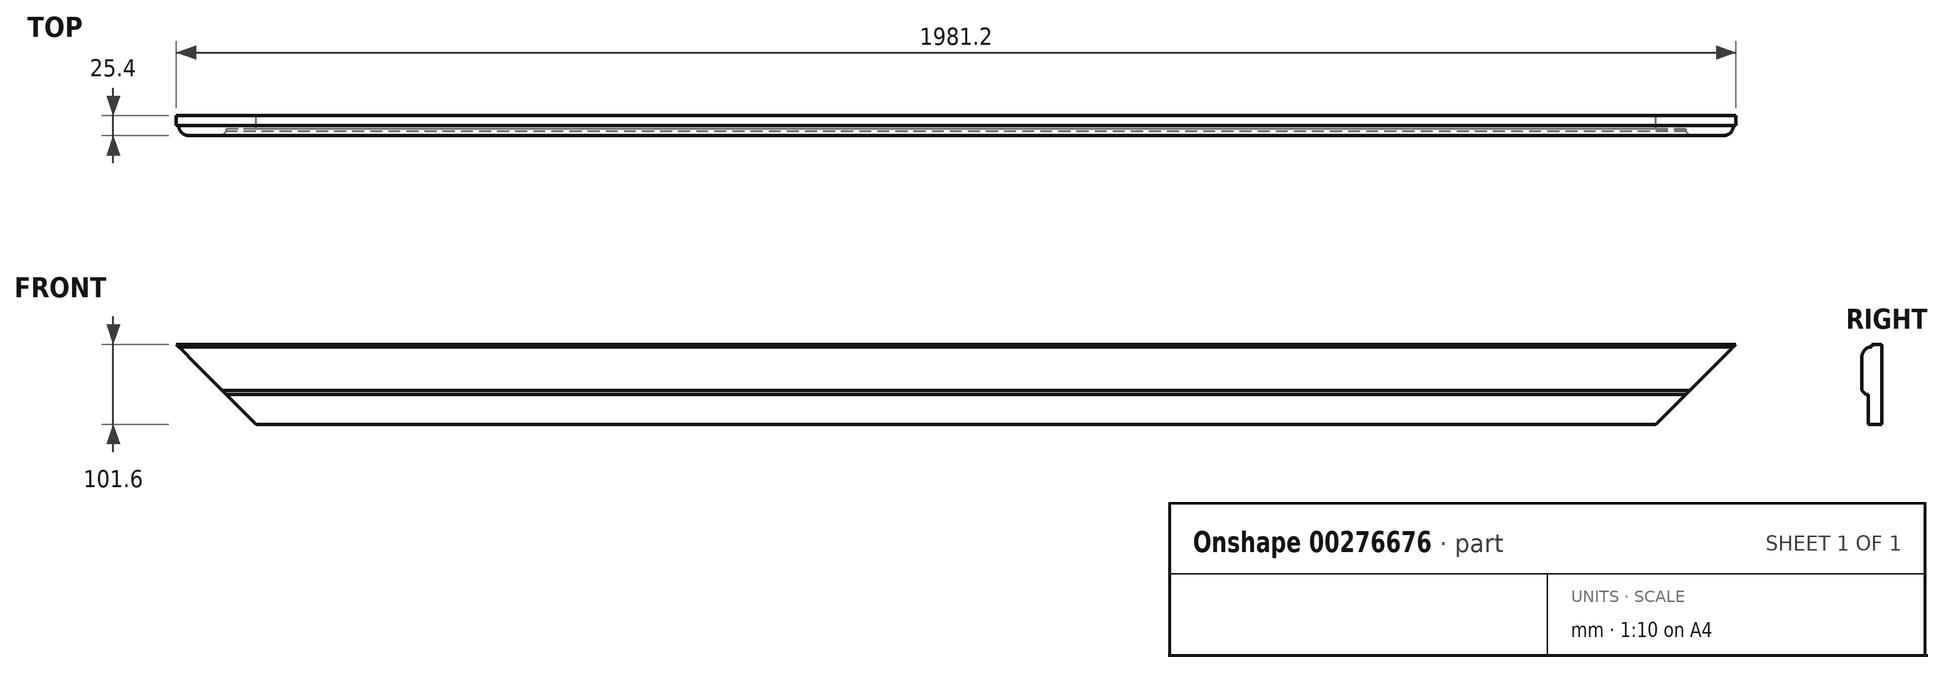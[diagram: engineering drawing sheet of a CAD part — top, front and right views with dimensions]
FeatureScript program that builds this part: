
annotation { "Feature Type Name" : "Feature", "Feature Type Description" : "" }
export const myFeature = defineFeature(function(context is Context, id is Id, definition is map)
    precondition{}
    {
        {
            var Q0;
            Q0=qCreatedBy(makeId("Right.planeOp"),FACE);
            var sketch = newSketch(context, id + "F0", { "sketchPlane" : qUnion([Q0])});
            skLineSegment(sketch, "E0.bottom", {"start": v(0, 0) * mm, "end": v(-17.14, 0) * mm});
            skLineSegment(sketch, "E0.top", {"start": v(0, 101.6) * mm, "end": v(-12.7, 101.6) * mm});
            skLineSegment(sketch, "E0.left", {"start": v(0, 0) * mm, "end": v(0, 101.6) * mm});
            skLineSegment(sketch, "E0.right", {"start": v(-25.4, 38.1) * mm, "end": v(-25.4, 85.72) * mm});
            skLineSegment(sketch, "E1", {"start": v(-17.14, 0) * mm, "end": v(-17.14, 38.1) * mm});
            skLineSegment(sketch, "E2", {"start": v(-17.14, 38.1) * mm, "end": v(-25.4, 38.1) * mm});
            skLineSegment(sketch, "E3", {"start": v(-12.7, 101.6) * mm, "end": v(-12.7, 98.42) * mm});
            skArc(sketch, "E4", {"start": v(-12.7, 98.43) * mm, "mid": v(-21.68, 94.7) * mm, "end": v(-25.4, 85.72) * mm});
            skSolve(sketch);
        }
        {
            var Q0;
            Q0=makeQuery(id+"F0.imprint","IMPRINT",FACE,{"disambiguationData":[TD([[makeQuery(id+"F0.imprint","IMPRINT",EDGE,{"derivedFrom":sQuery(id+"F0.wireOp",EDGE,"E0.bottom")}),-1.0]])]});
            extrude(context, id + "F1", {"entities" : qUnion([Q0]), "depth" : 1981.2 * mm});
        }
        {
            var Q0;
            Q0=makeQuery(id+"F1.opExtrude","SWEPT_FACE",FACE,{"disambiguationData":[OSD([sQuery(id+"F0.wireOp",EDGE,"E0.left")])]});
            var sketch = newSketch(context, id + "F2", { "sketchPlane" : qUnion([Q0])});
            skLineSegment(sketch, "E5", {"start": v(-1981.2, 101.6) * mm, "end": v(-1879.6, 0) * mm});
            skLineSegment(sketch, "E6", {"start": v(0, 101.6) * mm, "end": v(-101.6, 0) * mm});
            skSolve(sketch);
        }
        {
            var Q0;
            Q0 = qSketchRegion(id + "F2", true);
            var Q1;
            {var subQ0=sQuery(id+"F2.wireOp",EDGE,"E5");Q1=makeQuery(id+"F2.imprint","IMPRINT",FACE,{"disambiguationData":[TD([[makeQuery(id+"F2.imprint","IMPRINT",EDGE,{"derivedFrom":subQ0}),-1.0]])]});}
            var Q2;
            {var subQ0=sQuery(id+"F2.wireOp",EDGE,"E6");Q2=makeQuery(id+"F2.imprint","IMPRINT",FACE,{"disambiguationData":[TD([[makeQuery(id+"F2.imprint","IMPRINT",EDGE,{"derivedFrom":subQ0}),1.0]])]});}
            extrude(context, id + "F3", {"entities" : qUnion([Q0, Q1, Q2]), "operationType" : NewBodyOperationType.REMOVE, "oppositeDirection" : true, "depth" : 25.4 * mm});
        }
        {
            var Q0;
            Q0=makeQuery(id+"F1.opExtrude","SWEPT_EDGE",EDGE,{"disambiguationData":[OSD([sQuery(id+"F0.wireOp",EDGE,"E0.right"),sQuery(id+"F0.wireOp",EDGE,"E2")])]});
            chamfer(context, id + "F4", {"entities" : qUnion([Q0]), "width" : 5.08 * mm, "tangentPropagation" : true});
        }
    });
